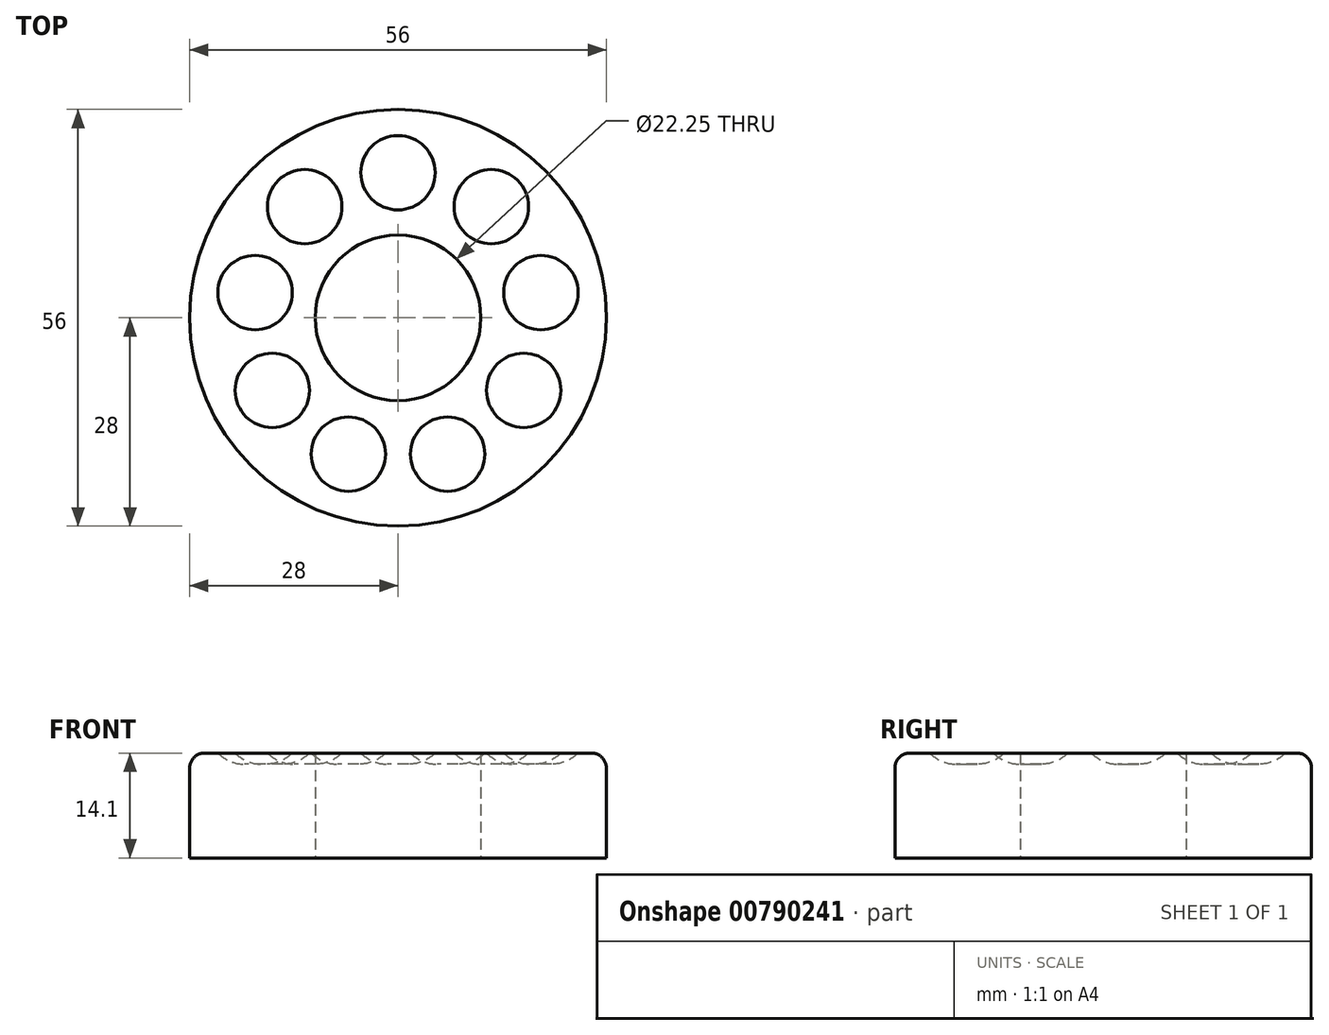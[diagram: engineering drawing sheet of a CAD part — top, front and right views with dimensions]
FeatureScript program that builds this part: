
annotation { "Feature Type Name" : "Feature", "Feature Type Description" : "" }
export const myFeature = defineFeature(function(context is Context, id is Id, definition is map)
    precondition{}
    {
        {
            var Q0;
            Q0=qCreatedBy(makeId("Top.planeOp"),FACE);
            var sketch = newSketch(context, id + "F0", { "sketchPlane" : qUnion([Q0])});
            skCircle(sketch, "E0", {"center": v(0, 0) * mm, "radius": 28 * mm});
            skCircle(sketch, "E1", {"center": v(0, 0) * mm, "radius": 11.12 * mm});
            skSolve(sketch);
        }
        {
            var Q0;
            Q0 = qSketchRegion(id + "F0", true);
            extrude(context, id + "F1", {"entities" : qUnion([Q0]), "depth" : 14.1 * mm, "offsetDistance" : 25 * mm});
        }
        {
            var Q0;
            Q0=makeQuery(id+"F1.opExtrude","CAP_EDGE",EDGE,{"disambiguationData":[OSD([sQuery(id+"F0.wireOp",EDGE,"E0")])],"isStart":false});
            fillet(context, id + "F2", {"entities" : qUnion([Q0]), "radius" : 2 * mm, "tangentPropagation" : true, "allowEdgeOverflow" : false});
        }
        {
            var Q0;
            Q0=makeQuery(id+"F1.opExtrude","CAP_FACE",FACE,{"disambiguationData":[OSD([sQuery(id+"F0.wireOp",EDGE,"E0"),sQuery(id+"F0.wireOp",EDGE,"E1")])],"isStart":false});
            var sketch = newSketch(context, id + "F3", { "sketchPlane" : qUnion([Q0])});
            skCircle(sketch, "E2", {"center": v(0, 19.5) * mm, "radius": 5 * mm});
            skCircle(sketch, "E3.1.0", {"center": v(-12.53, 14.94) * mm, "radius": 5 * mm});
            skCircle(sketch, "E3.2.0", {"center": v(-19.2, 3.39) * mm, "radius": 5 * mm});
            skCircle(sketch, "E3.3.0", {"center": v(-16.89, -9.75) * mm, "radius": 5 * mm});
            skCircle(sketch, "E3.4.0", {"center": v(-6.67, -18.32) * mm, "radius": 5 * mm});
            skCircle(sketch, "E3.5.0", {"center": v(6.67, -18.32) * mm, "radius": 5 * mm});
            skCircle(sketch, "E3.6.0", {"center": v(16.89, -9.75) * mm, "radius": 5 * mm});
            skCircle(sketch, "E3.7.0", {"center": v(19.2, 3.39) * mm, "radius": 5 * mm});
            skCircle(sketch, "E3.8.0", {"center": v(12.53, 14.94) * mm, "radius": 5 * mm});
            skPoint(sketch, "E3.center", {"position": v(0, 0) * mm});
            skSolve(sketch);
        }
        {
            var Q0;
            Q0 = qSketchRegion(id + "F3", true);
            extrude(context, id + "F4", {"entities" : qUnion([Q0]), "operationType" : NewBodyOperationType.REMOVE, "oppositeDirection" : true, "depth" : 1.5 * mm, "offsetDistance" : 25 * mm});
        }
        {
            var Q0;
            Q0=makeQuery(id+"F4.boolean.opBoolean","COPY",FACE,{"derivedFrom":makeQuery(id+"F4.opExtrude","CAP_FACE",FACE,{"disambiguationData":[OSD([sQuery(id+"F3.wireOp",EDGE,"E2")])],"isStart":false})});
            var Q1;
            Q1=makeQuery(id+"F4.boolean.opBoolean","COPY",FACE,{"derivedFrom":makeQuery(id+"F4.opExtrude","CAP_FACE",FACE,{"disambiguationData":[OSD([sQuery(id+"F3.wireOp",EDGE,"E3.1.0")])],"isStart":false})});
            var Q2;
            Q2=makeQuery(id+"F4.boolean.opBoolean","COPY",FACE,{"derivedFrom":makeQuery(id+"F4.opExtrude","CAP_FACE",FACE,{"disambiguationData":[OSD([sQuery(id+"F3.wireOp",EDGE,"E3.2.0")])],"isStart":false})});
            var Q3;
            Q3=makeQuery(id+"F4.boolean.opBoolean","COPY",FACE,{"derivedFrom":makeQuery(id+"F4.opExtrude","CAP_FACE",FACE,{"disambiguationData":[OSD([sQuery(id+"F3.wireOp",EDGE,"E3.3.0")])],"isStart":false})});
            var Q4;
            Q4=makeQuery(id+"F4.boolean.opBoolean","COPY",FACE,{"derivedFrom":makeQuery(id+"F4.opExtrude","CAP_FACE",FACE,{"disambiguationData":[OSD([sQuery(id+"F3.wireOp",EDGE,"E3.4.0")])],"isStart":false})});
            var Q5;
            Q5=makeQuery(id+"F4.boolean.opBoolean","COPY",FACE,{"derivedFrom":makeQuery(id+"F4.opExtrude","CAP_FACE",FACE,{"disambiguationData":[OSD([sQuery(id+"F3.wireOp",EDGE,"E3.5.0")])],"isStart":false})});
            var Q6;
            Q6=makeQuery(id+"F4.boolean.opBoolean","COPY",FACE,{"derivedFrom":makeQuery(id+"F4.opExtrude","CAP_FACE",FACE,{"disambiguationData":[OSD([sQuery(id+"F3.wireOp",EDGE,"E3.6.0")])],"isStart":false})});
            var Q7;
            Q7=makeQuery(id+"F4.boolean.opBoolean","COPY",FACE,{"derivedFrom":makeQuery(id+"F4.opExtrude","CAP_FACE",FACE,{"disambiguationData":[OSD([sQuery(id+"F3.wireOp",EDGE,"E3.7.0")])],"isStart":false})});
            var Q8;
            Q8=makeQuery(id+"F4.boolean.opBoolean","COPY",FACE,{"derivedFrom":makeQuery(id+"F4.opExtrude","CAP_FACE",FACE,{"disambiguationData":[OSD([sQuery(id+"F3.wireOp",EDGE,"E3.8.0")])],"isStart":false})});
            fillet(context, id + "F5", {"entities" : qUnion([Q0, Q1, Q2, Q3, Q4, Q5, Q6, Q7, Q8]), "radius" : 5 * mm, "tangentPropagation" : true, "allowEdgeOverflow" : false});
        }
    });
